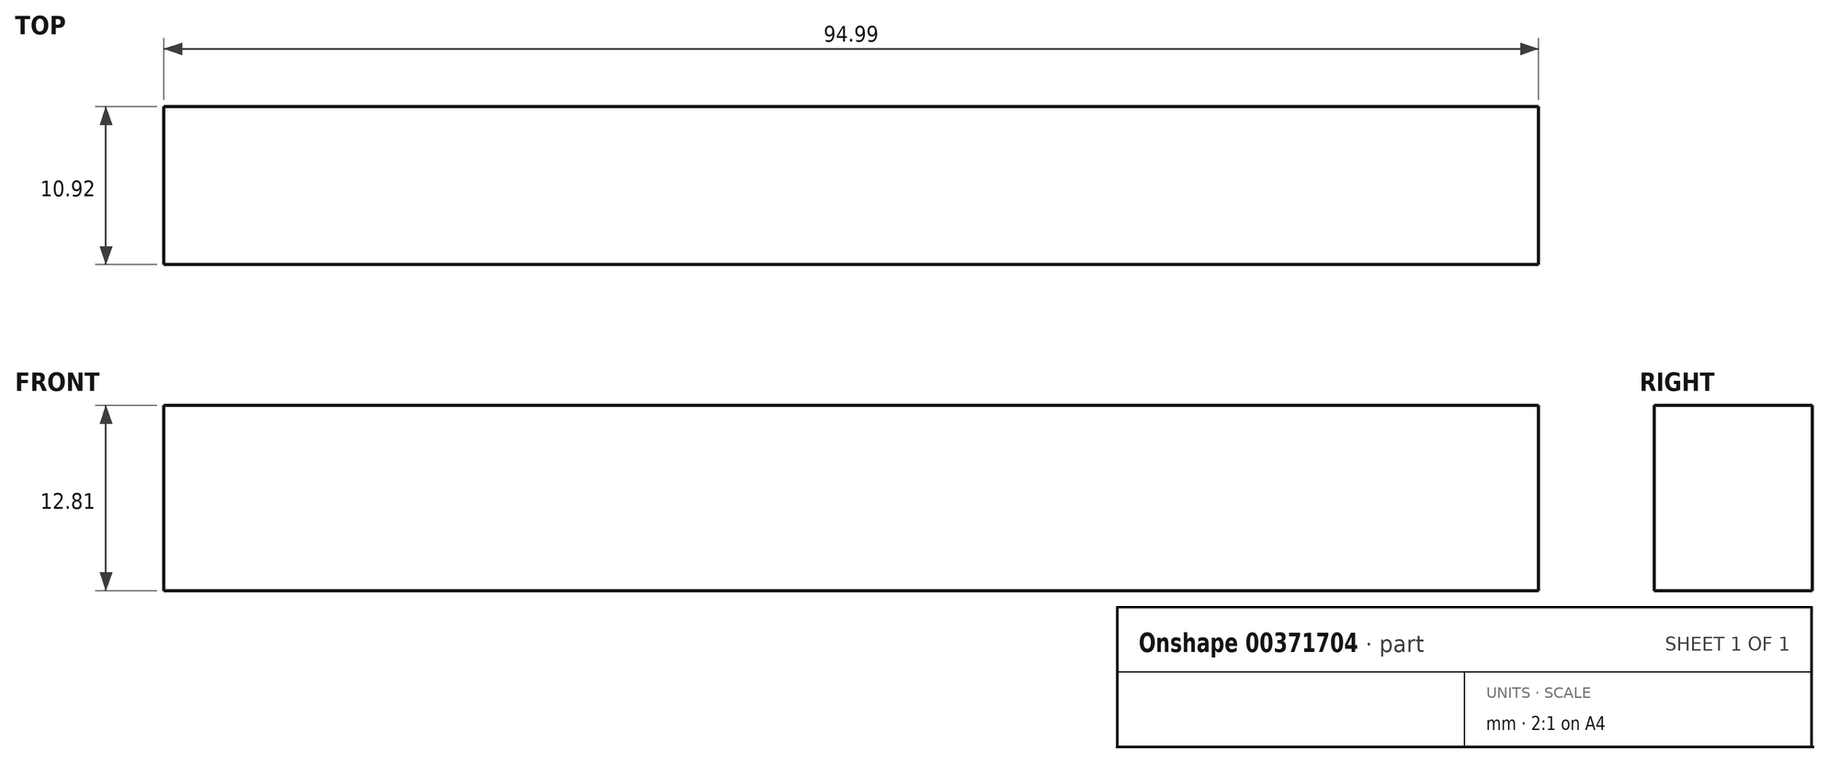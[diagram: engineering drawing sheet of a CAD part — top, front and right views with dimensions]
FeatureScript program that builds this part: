
annotation { "Feature Type Name" : "Feature", "Feature Type Description" : "" }
export const myFeature = defineFeature(function(context is Context, id is Id, definition is map)
    precondition{}
    {
        {
            var Q0;
            Q0=qCreatedBy(makeId("Front.planeOp"),FACE);
            var sketch = newSketch(context, id + "F0", { "sketchPlane" : qUnion([Q0])});
            skLineSegment(sketch, "E0.bottom", {"start": v(-61.87, -20.12) * mm, "end": v(33.12, -20.12) * mm});
            skLineSegment(sketch, "E0.top", {"start": v(-61.87, -32.93) * mm, "end": v(33.12, -32.93) * mm});
            skLineSegment(sketch, "E0.left", {"start": v(-61.87, -20.12) * mm, "end": v(-61.87, -32.93) * mm});
            skLineSegment(sketch, "E0.right", {"start": v(33.12, -20.12) * mm, "end": v(33.12, -32.93) * mm});
            skSolve(sketch);
        }
        {
            var Q0;
            Q0=makeQuery(id+"F0.imprint","IMPRINT",FACE,{"disambiguationData":[TD([[makeQuery(id+"F0.imprint","IMPRINT",EDGE,{"derivedFrom":sQuery(id+"F0.wireOp",EDGE,"E0.bottom")}),-1.0]])]});
            extrude(context, id + "F1", {"entities" : qUnion([Q0]), "depth" : 10.92 * mm});
        }
    });
